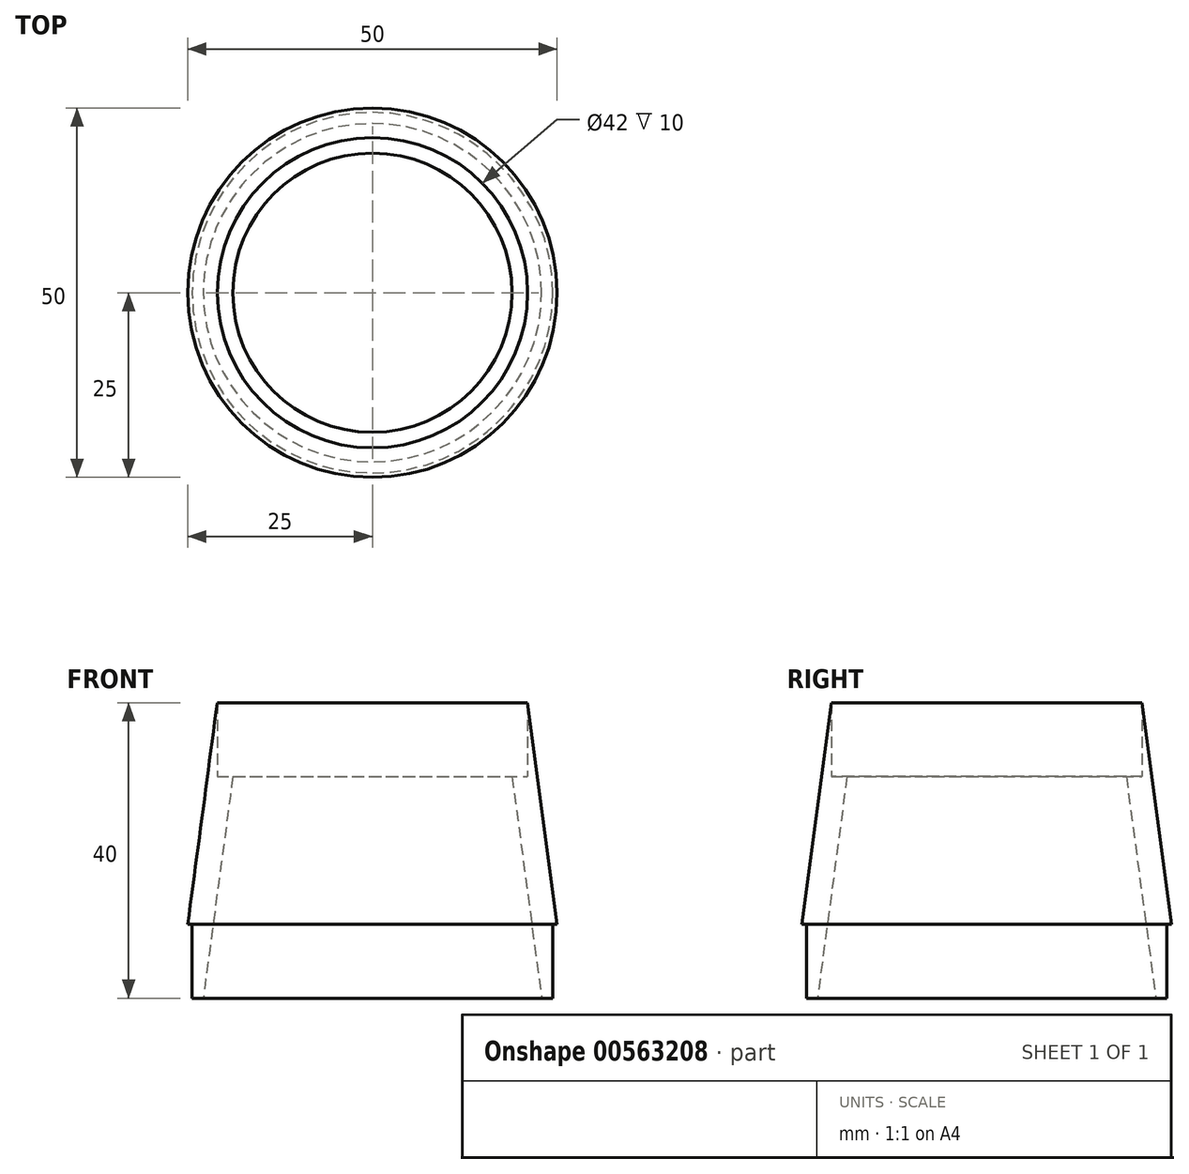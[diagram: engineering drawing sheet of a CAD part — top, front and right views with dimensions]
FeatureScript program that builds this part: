
annotation { "Feature Type Name" : "Feature", "Feature Type Description" : "" }
export const myFeature = defineFeature(function(context is Context, id is Id, definition is map)
    precondition{}
    {
        {
            var Q0;
            Q0=qCreatedBy(makeId("Front.planeOp"),FACE);
            var sketch = newSketch(context, id + "F0", { "sketchPlane" : qUnion([Q0])});
            skLineSegment(sketch, "E0", {"start": v(-24.4, 0) * mm, "end": v(-24.4, 10) * mm});
            skLineSegment(sketch, "E1", {"start": v(-24.4, 10) * mm, "end": v(-25, 10) * mm});
            skLineSegment(sketch, "E2", {"start": v(-25, 10) * mm, "end": v(-21, 40) * mm});
            skLineSegment(sketch, "E3", {"start": v(-21, 40) * mm, "end": v(-21, 30) * mm});
            skLineSegment(sketch, "E4", {"start": v(-21, 30) * mm, "end": v(-18.9, 30) * mm});
            skLineSegment(sketch, "E5", {"start": v(-24.4, 0) * mm, "end": v(-22.9, 0) * mm});
            skLineSegment(sketch, "E6", {"start": v(-22.9, 0) * mm, "end": v(-18.9, 30) * mm});
            skLineSegment(sketch, "E7", {"start": v(0, 0) * mm, "end": v(0, 40) * mm});
            skSolve(sketch);
        }
        {
            var Q0;
            Q0=makeQuery(id+"F0.imprint","IMPRINT",FACE,{"disambiguationData":[TD([[makeQuery(id+"F0.imprint","IMPRINT",EDGE,{"derivedFrom":sQuery(id+"F0.wireOp",EDGE,"LMcC42V6-Fvrw-CDMh-v5W1-le1EN8qKH68T")}),-1.0]])]});
            var Q1;
            Q1=makeQuery(id+"F0.imprint","IMPRINT",FACE,{"disambiguationData":[TD([[makeQuery(id+"F0.imprint","IMPRINT",EDGE,{"derivedFrom":sQuery(id+"F0.wireOp",EDGE,"E0")}),-1.0]])]});
            var Q2;
            Q2=sQuery(id+"F0.wireOp",EDGE,"E7");
            revolve(context, id + "F1", {"entities" : qUnion([Q0, Q1]), "axis" : qUnion([Q2]), "revolveType" : RevolveType.FULL});
        }
    });
